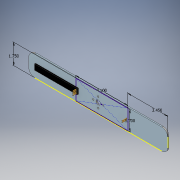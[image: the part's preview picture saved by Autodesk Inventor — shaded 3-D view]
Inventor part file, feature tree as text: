
AUTODESK INVENTOR PART (.ipt)
format: ipt  version: 2016 (Build 200138000, 138)  size: 223,744 bytes
history: native  units: in
note: dims shown in document units (in); Inventor stores cm internally (conversion verified against a paired STEP export)
features: sketch x7, extrude x6, fillet x1
ambient origin geometry x8: Origin, YZ Plane, XZ Plane, XY Plane, X Axis, Y Axis, Z Axis, Center Point
bodies: Solid1 (feature_tree)
feature tree (14):
  extrude  "Extrusion1"  Depth=1.8in
  extrude  "Extrusion2"  Depth=0.11in
  extrude  "Extrusion3"  Depth=3.7in
  extrude  "Extrusion4"  Depth=0.3937in
  extrude  "Extrusion5"  Depth=0.1in TaperAngle=0.0deg
  fillet  "Fillet1"  Radius=0.75in
  extrude  "Extrusion6"  Depth=0.5in
  sketch  "Sketch9"  dims[d37=0.133in d38=0.133in d39=0.133in d40=0.133in d45=0.35in d46=0.0in d47=0.37in d48=0.39in d49=0.95in d50=0.127in d51=0.0in d56=0.65in d57=0.5794in d58=0.0811in d59=0.0742in d60=0.0434in d63=0.0811in d64=0.0742in d65=4.2361in d66=4.1618in d67=4.2361in d68=0.6472in d69=4.5in d70=1.7in d73=0.5in d76=1.75in d77=3.45in]
  sketch  "Sketch1"  dims[d0=12.0in d1=1.8in]
  sketch  "Sketch2"  dims[d2=0.11in d3=0.0in d4=3.0in]
  sketch  "Sketch5"  dims[d7=0.474in d8=1.5748in d10=0.105in d11=0.3937in d13=1.0in]
  sketch  "Sketch6"  dims[d15=0.4in d16=0.0in]
  sketch  "Sketch8"  dims[d17=3.0in d18=1.4in d19=3.7in d20=0.474in d21=0.105in d22=1.0in d25=0.1in d26=0.0in d35=0.75in d36=0.0in]
  sketch  "Sketch3"  dims[d5=1.4in d6=3.7in]
